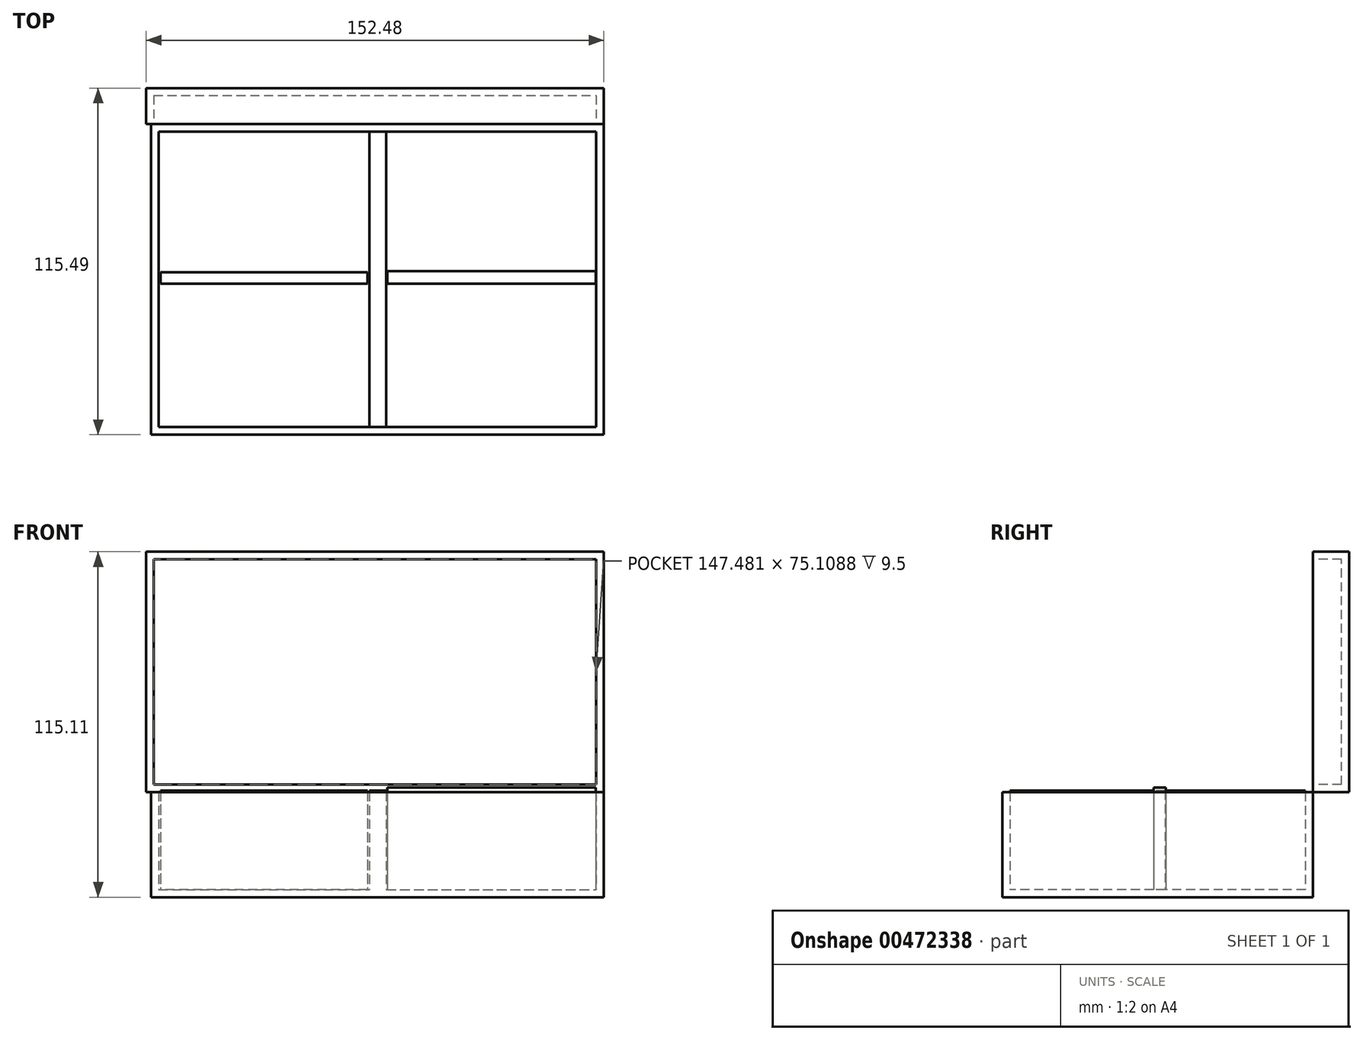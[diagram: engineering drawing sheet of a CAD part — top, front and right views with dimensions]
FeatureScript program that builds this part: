
annotation { "Feature Type Name" : "Feature", "Feature Type Description" : "" }
export const myFeature = defineFeature(function(context is Context, id is Id, definition is map)
    precondition{}
    {
        {
            var Q0;
            Q0=qCreatedBy(makeId("Top.planeOp"),FACE);
            var sketch = newSketch(context, id + "F0", { "sketchPlane" : qUnion([Q0])});
            skLineSegment(sketch, "E0.bottom", {"start": v(-75.49, -30.49) * mm, "end": v(75.37, -30.49) * mm});
            skLineSegment(sketch, "E0.top", {"start": v(-75.49, 73) * mm, "end": v(75.37, 73) * mm});
            skLineSegment(sketch, "E0.left", {"start": v(-75.49, -30.49) * mm, "end": v(-75.49, 73) * mm});
            skLineSegment(sketch, "E0.right", {"start": v(75.37, -30.49) * mm, "end": v(75.37, 73) * mm});
            skSolve(sketch);
        }
        {
            var Q0;
            Q0=makeQuery(id+"F0.imprint","IMPRINT",FACE,{"disambiguationData":[TD([[makeQuery(id+"F0.imprint","IMPRINT",EDGE,{"derivedFrom":sQuery(id+"F0.wireOp",EDGE,"E0.bottom")}),1.0]])]});
            extrude(context, id + "F1", {"entities" : qUnion([Q0]), "depth" : 35 * mm});
        }
        {
            var Q0;
            Q0=makeQuery(id+"F1.opExtrude","CAP_FACE",FACE,{"disambiguationData":[OSD([sQuery(id+"F0.wireOp",EDGE,"E0.bottom"),sQuery(id+"F0.wireOp",EDGE,"E0.top"),sQuery(id+"F0.wireOp",EDGE,"E0.left"),sQuery(id+"F0.wireOp",EDGE,"E0.right")])],"isStart":false});
            shell(context, id + "F2", {"entities" : qUnion([Q0]), "thickness" : 2.5 * mm});
        }
        {
            var Q0;
            Q0=makeQuery(id+"F2.opShell","OFFSET_FACE",FACE,{"disambiguationData":[OSD([sQuery(id+"F0.wireOp",EDGE,"E0.bottom"),sQuery(id+"F0.wireOp",EDGE,"E0.top"),sQuery(id+"F0.wireOp",EDGE,"E0.left"),sQuery(id+"F0.wireOp",EDGE,"E0.right")])]});
            var sketch = newSketch(context, id + "F3", { "sketchPlane" : qUnion([Q0])});
            skLineSegment(sketch, "E1.bottom", {"start": v(-2.72, 70.5) * mm, "end": v(2.9, 70.5) * mm});
            skLineSegment(sketch, "E1.top", {"start": v(-2.72, -27.99) * mm, "end": v(2.9, -27.99) * mm});
            skLineSegment(sketch, "E1.left", {"start": v(-2.72, 70.5) * mm, "end": v(-2.72, -27.99) * mm});
            skLineSegment(sketch, "E1.right", {"start": v(2.9, 70.5) * mm, "end": v(2.9, -27.99) * mm});
            skSolve(sketch);
        }
        {
            var Q0;
            {var subQ0=sQuery(id+"F3.wireOp",EDGE,"E1.left");Q0=makeQuery(id+"F3.imprint","IMPRINT",FACE,{"disambiguationData":[TD([[makeQuery(id+"F3.imprint","IMPRINT",EDGE,{"derivedFrom":subQ0}),-1.0]])]});}
            var sketch = newSketch(context, id + "F4", { "sketchPlane" : qUnion([Q0])});
            skLineSegment(sketch, "E2.bottom", {"start": v(-3.31, 23.68) * mm, "end": v(-72.3, 23.68) * mm});
            skLineSegment(sketch, "E2.top", {"start": v(-3.31, 19.84) * mm, "end": v(-72.3, 19.84) * mm});
            skLineSegment(sketch, "E2.left", {"start": v(-3.31, 23.68) * mm, "end": v(-3.31, 19.84) * mm});
            skLineSegment(sketch, "E2.right", {"start": v(-72.3, 23.68) * mm, "end": v(-72.3, 19.84) * mm});
            skSolve(sketch);
        }
        {
            var Q0;
            {var subQ0=sQuery(id+"F3.wireOp",EDGE,"E1.right");Q0=makeQuery(id+"F3.imprint","IMPRINT",FACE,{"disambiguationData":[TD([[makeQuery(id+"F3.imprint","IMPRINT",EDGE,{"derivedFrom":subQ0}),1.0]])]});}
            var sketch = newSketch(context, id + "F5", { "sketchPlane" : qUnion([Q0])});
            skLineSegment(sketch, "E3.bottom", {"start": v(3.2, 23.98) * mm, "end": v(72.77, 23.98) * mm});
            skLineSegment(sketch, "E3.top", {"start": v(3.2, 19.84) * mm, "end": v(72.77, 19.84) * mm});
            skLineSegment(sketch, "E3.left", {"start": v(3.2, 23.98) * mm, "end": v(3.2, 19.84) * mm});
            skLineSegment(sketch, "E3.right", {"start": v(72.77, 23.98) * mm, "end": v(72.77, 19.84) * mm});
            skSolve(sketch);
        }
        {
            var Q0;
            Q0 = qSketchRegion(id + "F3", true);
            extrude(context, id + "F6", {"entities" : qUnion([Q0]), "operationType" : NewBodyOperationType.ADD, "depth" : 33 * mm});
        }
        {
            var Q0;
            Q0 = qSketchRegion(id + "F5", true);
            extrude(context, id + "F7", {"entities" : qUnion([Q0]), "operationType" : NewBodyOperationType.ADD, "depth" : 34 * mm});
        }
        {
            var Q0;
            Q0 = qSketchRegion(id + "F4", true);
            extrude(context, id + "F8", {"entities" : qUnion([Q0]), "operationType" : NewBodyOperationType.ADD, "depth" : 33 * mm});
        }
        {
            var Q0;
            Q0=makeQuery(id+"F1.opExtrude","SWEPT_FACE",FACE,{"disambiguationData":[OSD([sQuery(id+"F0.wireOp",EDGE,"E0.top")])]});
            var sketch = newSketch(context, id + "F9", { "sketchPlane" : qUnion([Q0])});
            skLineSegment(sketch, "E4.bottom", {"start": v(-75.37, 35) * mm, "end": v(77.11, 35) * mm});
            skLineSegment(sketch, "E4.top", {"start": v(-75.37, 115.1) * mm, "end": v(77.11, 115.1) * mm});
            skLineSegment(sketch, "E4.left", {"start": v(-75.37, 35) * mm, "end": v(-75.37, 115.1) * mm});
            skLineSegment(sketch, "E4.right", {"start": v(77.11, 35) * mm, "end": v(77.11, 115.1) * mm});
            skSolve(sketch);
        }
        {
            var Q0;
            Q0=makeQuery(id+"F9.imprint","IMPRINT",FACE,{"disambiguationData":[TD([[makeQuery(id+"F9.imprint","IMPRINT",EDGE,{"derivedFrom":sQuery(id+"F9.wireOp",EDGE,"E4.top")}),-1.0]])]});
            extrude(context, id + "F10", {"entities" : qUnion([Q0]), "depth" : 12 * mm});
        }
        {
            var Q0;
            Q0=makeQuery(id+"F10.opExtrude","CAP_FACE",FACE,{"disambiguationData":[OSD([sQuery(id+"F9.wireOp",EDGE,"E4.bottom"),sQuery(id+"F9.wireOp",EDGE,"E4.top"),sQuery(id+"F9.wireOp",EDGE,"E4.left"),sQuery(id+"F9.wireOp",EDGE,"E4.right")])],"isStart":true});
            shell(context, id + "F11", {"entities" : qUnion([Q0]), "thickness" : 2.5 * mm});
        }
    });
